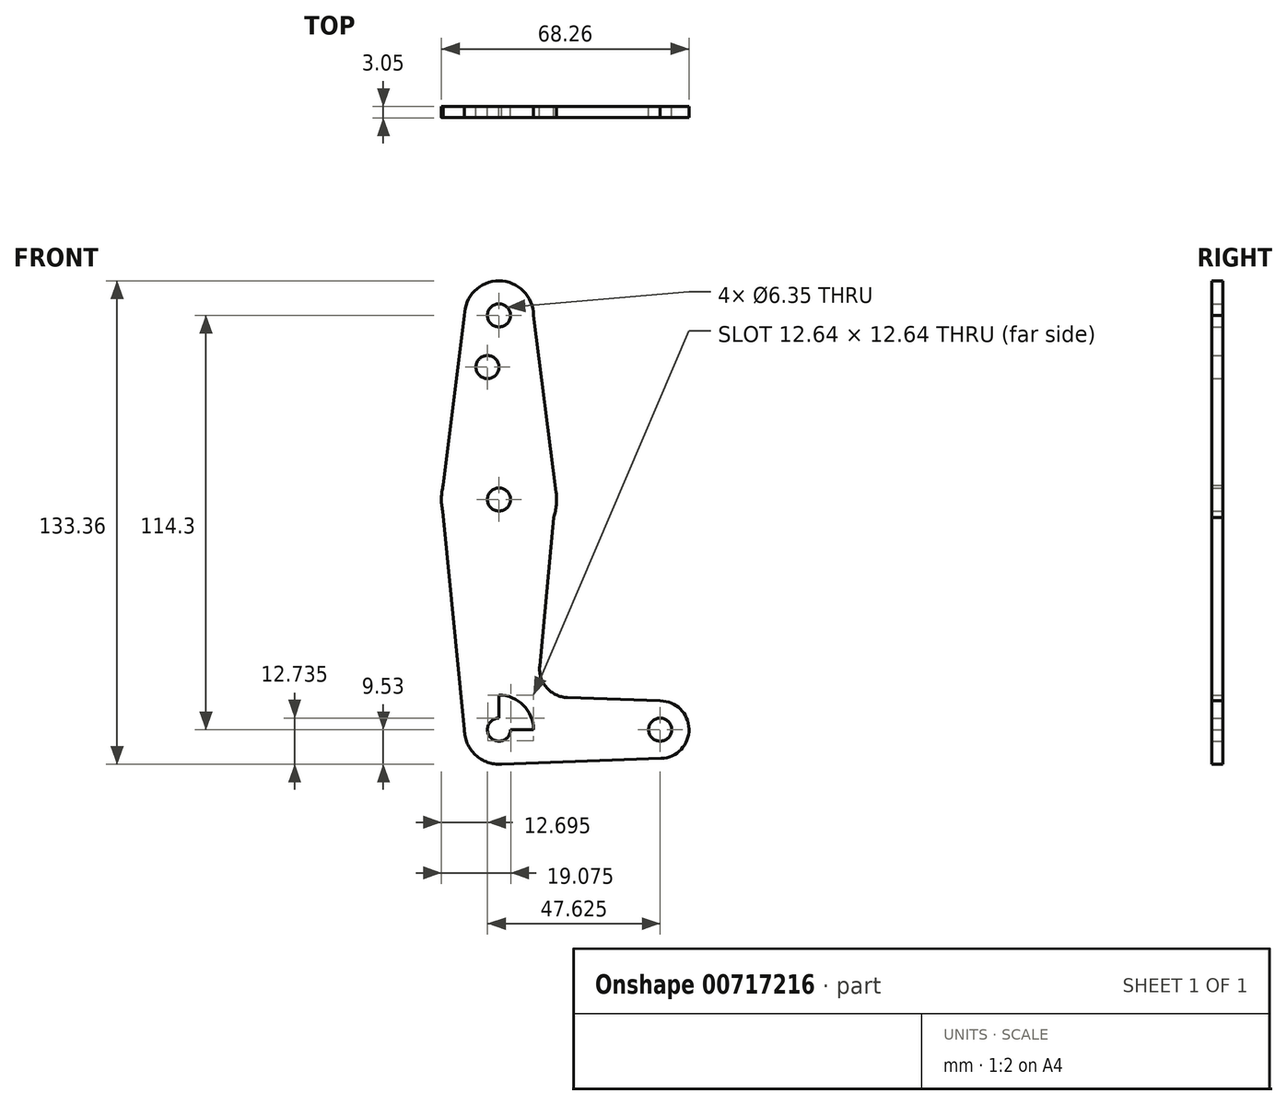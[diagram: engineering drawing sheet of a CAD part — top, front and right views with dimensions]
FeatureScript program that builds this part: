
annotation { "Feature Type Name" : "Feature", "Feature Type Description" : "" }
export const myFeature = defineFeature(function(context is Context, id is Id, definition is map)
    precondition{}
    {
        {
            var Q0;
            Q0=qCreatedBy(makeId("Front.planeOp"),FACE);
            var sketch = newSketch(context, id + "F0", { "sketchPlane" : qUnion([Q0])});
            skLineSegment(sketch, "E0", {"start": v(0, 0) * mm, "end": v(0, 114.3) * mm});
            skLineSegment(sketch, "E1", {"start": v(0, 114.3) * mm, "end": v(0, 0) * mm});
            skLineSegment(sketch, "E2", {"start": v(0, 0) * mm, "end": v(44.45, 0) * mm});
            skCircle(sketch, "E3", {"center": v(44.45, 0) * mm, "radius": 7.94 * mm});
            skCircle(sketch, "E4", {"center": v(0, 63.5) * mm, "radius": 15.88 * mm});
            skCircle(sketch, "E5", {"center": v(0, 114.3) * mm, "radius": 9.53 * mm});
            skCircle(sketch, "E6", {"center": v(0, 0) * mm, "radius": 9.53 * mm});
            skLineSegment(sketch, "E7", {"start": v(9.52, 114.3) * mm, "end": v(15.75, 65.5) * mm});
            skLineSegment(sketch, "E8", {"start": v(15.75, 65.5) * mm, "end": v(11.22, 17.55) * mm});
            skLineSegment(sketch, "E9", {"start": v(0, -9.53) * mm, "end": v(44.73, -7.93) * mm});
            skCircle(sketch, "E10", {"center": v(0, 114.3) * mm, "radius": 3.18 * mm});
            skCircle(sketch, "E11", {"center": v(-3.18, 100.03) * mm, "radius": 3.18 * mm});
            skCircle(sketch, "E12", {"center": v(0, 63.5) * mm, "radius": 3.17 * mm});
            skCircle(sketch, "E13", {"center": v(0, 0) * mm, "radius": 3.18 * mm});
            skCircle(sketch, "E14", {"center": v(44.45, 0) * mm, "radius": 3.18 * mm});
            skLineSegment(sketch, "E15", {"start": v(-15.87, 63.5) * mm, "end": v(-9.53, 0) * mm});
            skLineSegment(sketch, "E16", {"start": v(-15.87, 63.5) * mm, "end": v(-9.53, 114.3) * mm});
            skArc(sketch, "E17.filletArc", {"start": v(11.22, 17.55) * mm, "mid": v(13.16, 11.55) * mm, "end": v(18.85, 8.85) * mm});
            skLineSegment(sketch, "E18", {"start": v(44.45, 7.94) * mm, "end": v(18.85, 8.85) * mm});
            skSolve(sketch);
        }
        {
            var Q0;
            Q0 = qSketchRegion(id + "F0", true);
            var Q1;
            {var subQ0=sQuery(id+"F0.wireOp",EDGE,"E6");var subQ1=sQuery(id+"F0.wireOp",EDGE,"E1");var subQ2=makeQuery(id+"F0.imprint","INTERSECT",VERTEX,{"derivedFrom":[subQ1,subQ0]});Q1=makeQuery(id+"F0.imprint","IMPRINT",FACE,{"disambiguationData":[TD([[makeQuery(id+"F0.imprint","IMPRINT",EDGE,{"disambiguationData":[TD([[subQ2,-1.0]])],"derivedFrom":subQ1}),1.0]])]});}
            extrude(context, id + "F1", {"entities" : qUnion([Q0, Q1]), "depth" : 3.05 * mm, "offsetDistance" : 25.4 * mm});
        }
    });
